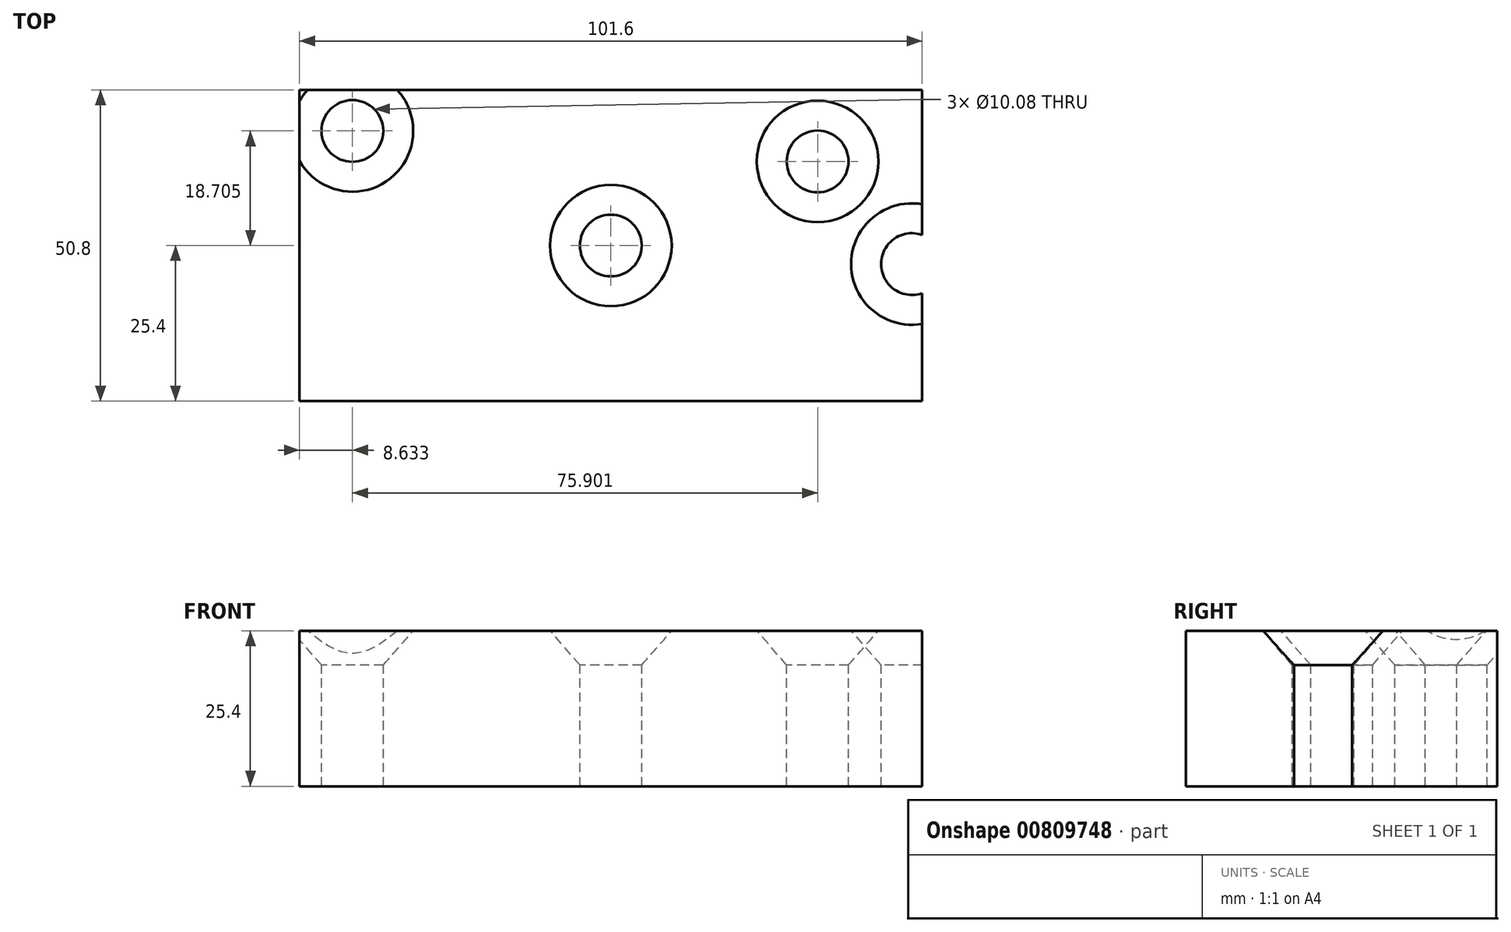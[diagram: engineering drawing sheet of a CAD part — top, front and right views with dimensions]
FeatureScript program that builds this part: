
annotation { "Feature Type Name" : "Feature", "Feature Type Description" : "" }
export const myFeature = defineFeature(function(context is Context, id is Id, definition is map)
    precondition{}
    {
        {
            var Q0;
            Q0=qCreatedBy(makeId("Top.planeOp"),FACE);
            var sketch = newSketch(context, id + "F0", { "sketchPlane" : qUnion([Q0])});
            skLineSegment(sketch, "E0.bottom", {"start": v(50.8, 25.4) * mm, "end": v(-50.8, 25.4) * mm});
            skLineSegment(sketch, "E0.top", {"start": v(50.8, -25.4) * mm, "end": v(-50.8, -25.4) * mm});
            skLineSegment(sketch, "E0.left", {"start": v(50.8, 25.4) * mm, "end": v(50.8, -25.4) * mm});
            skLineSegment(sketch, "E0.right", {"start": v(-50.8, 25.4) * mm, "end": v(-50.8, -25.4) * mm});
            skPoint(sketch, "E0.middle", {"position": v(0, 0) * mm});
            skSolve(sketch);
        }
        {
            var Q0;
            Q0=makeQuery(id+"F0.imprint","IMPRINT",FACE,{"disambiguationData":[TD([[makeQuery(id+"F0.imprint","IMPRINT",EDGE,{"derivedFrom":sQuery(id+"F0.wireOp",EDGE,"E0.bottom")}),1.0]])]});
            extrude(context, id + "F1", {"entities" : qUnion([Q0]), "depth" : 25.4 * mm, "offsetDistance" : 25.4 * mm});
        }
        {
            var Q0;
            Q0=makeQuery(id+"F1.opExtrude","CAP_FACE",FACE,{"disambiguationData":[OSD([sQuery(id+"F0.wireOp",EDGE,"E0.bottom"),sQuery(id+"F0.wireOp",EDGE,"E0.top"),sQuery(id+"F0.wireOp",EDGE,"E0.left"),sQuery(id+"F0.wireOp",EDGE,"E0.right")])],"isStart":false});
            var sketch = newSketch(context, id + "F2", { "sketchPlane" : qUnion([Q0])});
            skSolve(sketch);
        }
        {
            var Q0;
            Q0=makeQuery(id+"F2.imprint","IMPRINT",FACE,{"disambiguationData":[TD([[makeQuery(id+"F2.imprint","IMPRINT",EDGE,{"derivedFrom":makeQuery(id+"F1.opExtrude","CAP_EDGE",EDGE,{"disambiguationData":[OSD([sQuery(id+"F0.wireOp",EDGE,"E0.bottom")])],"isStart":false})}),1.0]])]});
            var sketch = newSketch(context, id + "F3", { "sketchPlane" : qUnion([Q0])});
            skPoint(sketch, "E1", {"position": v(-42.17, 18.7) * mm});
            skPoint(sketch, "E2", {"position": v(49.13, -3.03) * mm});
            skLineSegment(sketch, "E3.bottom", {"start": v(33.73, 13.73) * mm, "end": v(-33.73, 13.73) * mm, "construction": true});
            skLineSegment(sketch, "E3.top", {"start": v(33.73, -13.73) * mm, "end": v(-33.73, -13.73) * mm, "construction": true});
            skLineSegment(sketch, "E3.left", {"start": v(33.73, 13.73) * mm, "end": v(33.73, -13.73) * mm, "construction": true});
            skLineSegment(sketch, "E3.right", {"start": v(-33.73, 13.73) * mm, "end": v(-33.73, -13.73) * mm, "construction": true});
            skPoint(sketch, "E3.middle", {"position": v(0, 0) * mm});
            skSolve(sketch);
        }
        {
            var Q0;
            Q0=sQuery(id+"F3.wireOp",VERTEX,"E1");
            var Q1;
            Q1=sQuery(id+"F3.wireOp",VERTEX,"E3.middle");
            var Q2;
            Q2=sQuery(id+"F3.wireOp",VERTEX,"E3.bottom.start");
            var Q3;
            Q3=sQuery(id+"F3.wireOp",VERTEX,"E2");
            var Q4;
            Q4=makeQuery(id+"F1.opExtrude","SWEPT_BODY",BODY,{"disambiguationData":[OSD([sQuery(id+"F0.wireOp",EDGE,"E0.bottom"),sQuery(id+"F0.wireOp",EDGE,"E0.top"),sQuery(id+"F0.wireOp",EDGE,"E0.left"),sQuery(id+"F0.wireOp",EDGE,"E0.right")])]});
            hole(context, id + "F4", {"style" : HoleStyle.C_SINK, "endStyle" : HoleEndStyle.THROUGH, "standardTappedOrClearance" : lookupTablePath({ "standard" : "ANSI", "fit" : "Normal (ASME)", "size" : "3/8", "type" : "Clearance" }), "standardBlindInLast" : lookupTablePath({ "fit" : "Free", "standard" : "ANSI", "size" : "3/8", "type" : "Clearance" }), "holeDiameter" : 10.08 * mm, "cSinkDiameter" : 19.84 * mm, "cSinkAngle" : 82 * degree, "majorDiameter" : 6.35 * mm, "isTappedThrough" : true, "tappedDepth" : 12.7 * mm, "tapClearance" : 3, "locations" : qUnion([Q0, Q1, Q2, Q3]), "scope" : qUnion([Q4])});
        }
    });
